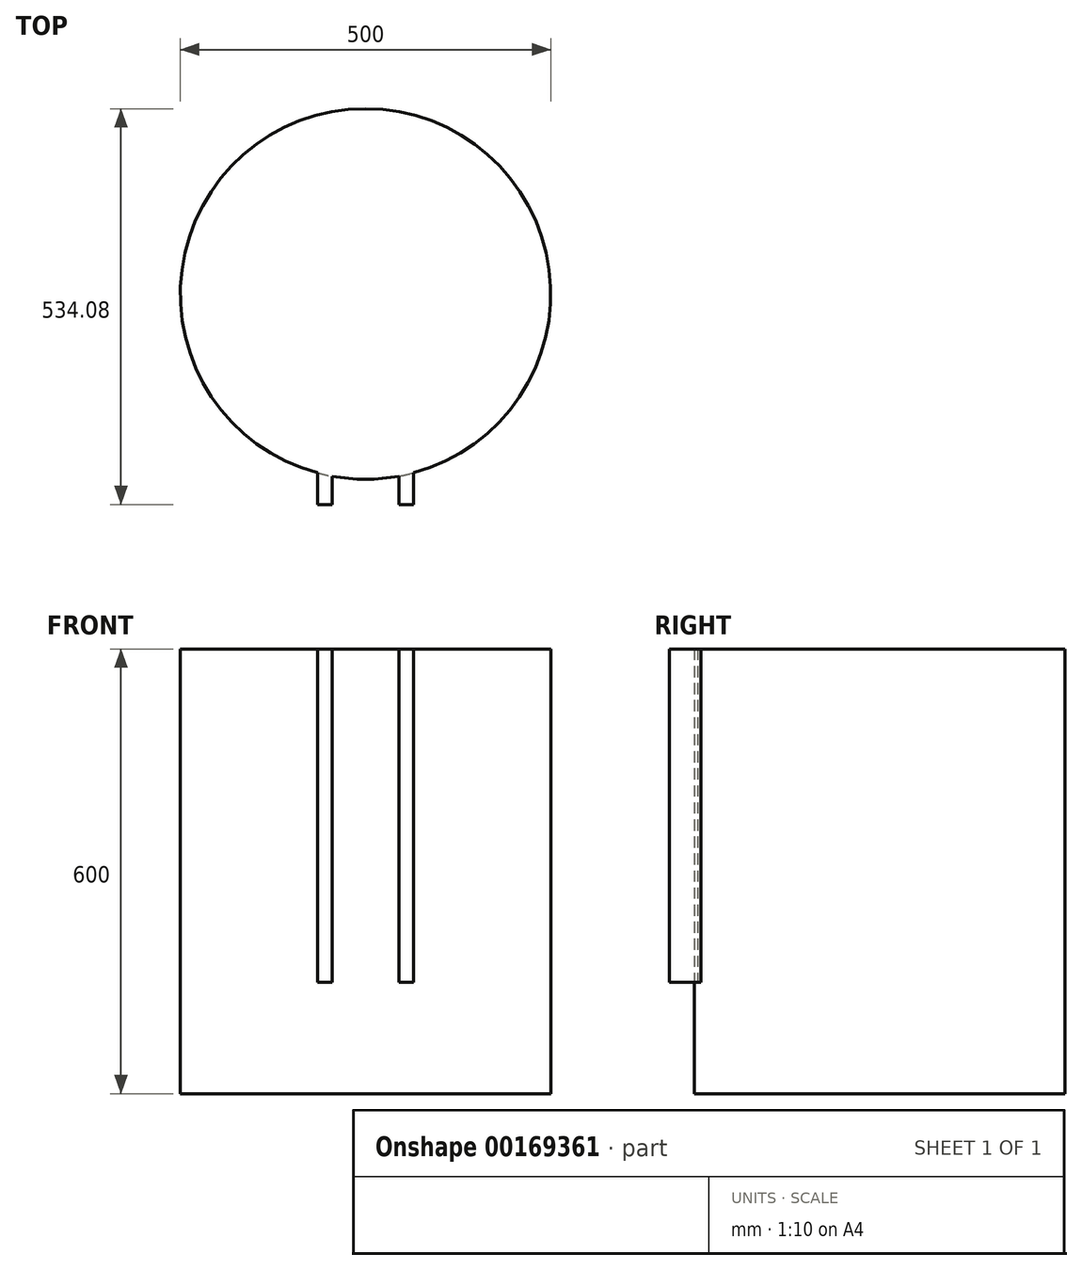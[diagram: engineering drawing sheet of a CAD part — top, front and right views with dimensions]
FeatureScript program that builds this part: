
annotation { "Feature Type Name" : "Feature", "Feature Type Description" : "" }
export const myFeature = defineFeature(function(context is Context, id is Id, definition is map)
    precondition{}
    {
        {
            var Q0;
            Q0=qCreatedBy(makeId("Top.planeOp"),FACE);
            var sketch = newSketch(context, id + "F0", { "sketchPlane" : qUnion([Q0])});
            skCircle(sketch, "E0", {"center": v(0, -15.92) * mm, "radius": 250 * mm});
            skSolve(sketch);
        }
        {
            var Q0;
            Q0=qSketchRegion(id+"F0",true);
            extrude(context, id + "F1", {"entities" : qUnion([Q0]), "depth" : 600 * mm});
        }
        {
            var Q0;
            Q0=qCreatedBy(makeId("Front.planeOp"),FACE);
            var sketch = newSketch(context, id + "F2", { "sketchPlane" : qUnion([Q0])});
            skLineSegment(sketch, "E1.bottom", {"start": v(45, 600) * mm, "end": v(65, 600) * mm});
            skLineSegment(sketch, "E1.top", {"start": v(45, 150) * mm, "end": v(65, 150) * mm});
            skLineSegment(sketch, "E1.left", {"start": v(45, 600) * mm, "end": v(45, 150) * mm});
            skLineSegment(sketch, "E1.right", {"start": v(65, 600) * mm, "end": v(65, 150) * mm});
            skPoint(sketch, "E2", {"position": v(65, 0) * mm});
            skLineSegment(sketch, "E3.MirrorCS", {"start": v(-45, 600) * mm, "end": v(-45, 150) * mm});
            skLineSegment(sketch, "E4.MirrorCS", {"start": v(-65, 600) * mm, "end": v(-65, 150) * mm});
            skLineSegment(sketch, "E5.MirrorCS", {"start": v(-45, 600) * mm, "end": v(-65, 600) * mm});
            skLineSegment(sketch, "E6.MirrorCS", {"start": v(-45, 150) * mm, "end": v(-65, 150) * mm});
            skSolve(sketch);
        }
        {
            var Q0;
            Q0=qSketchRegion(id+"F2",true);
            extrude(context, id + "F3", {"entities" : qUnion([Q0]), "operationType" : NewBodyOperationType.ADD, "depth" : 300 * mm});
        }
    });
